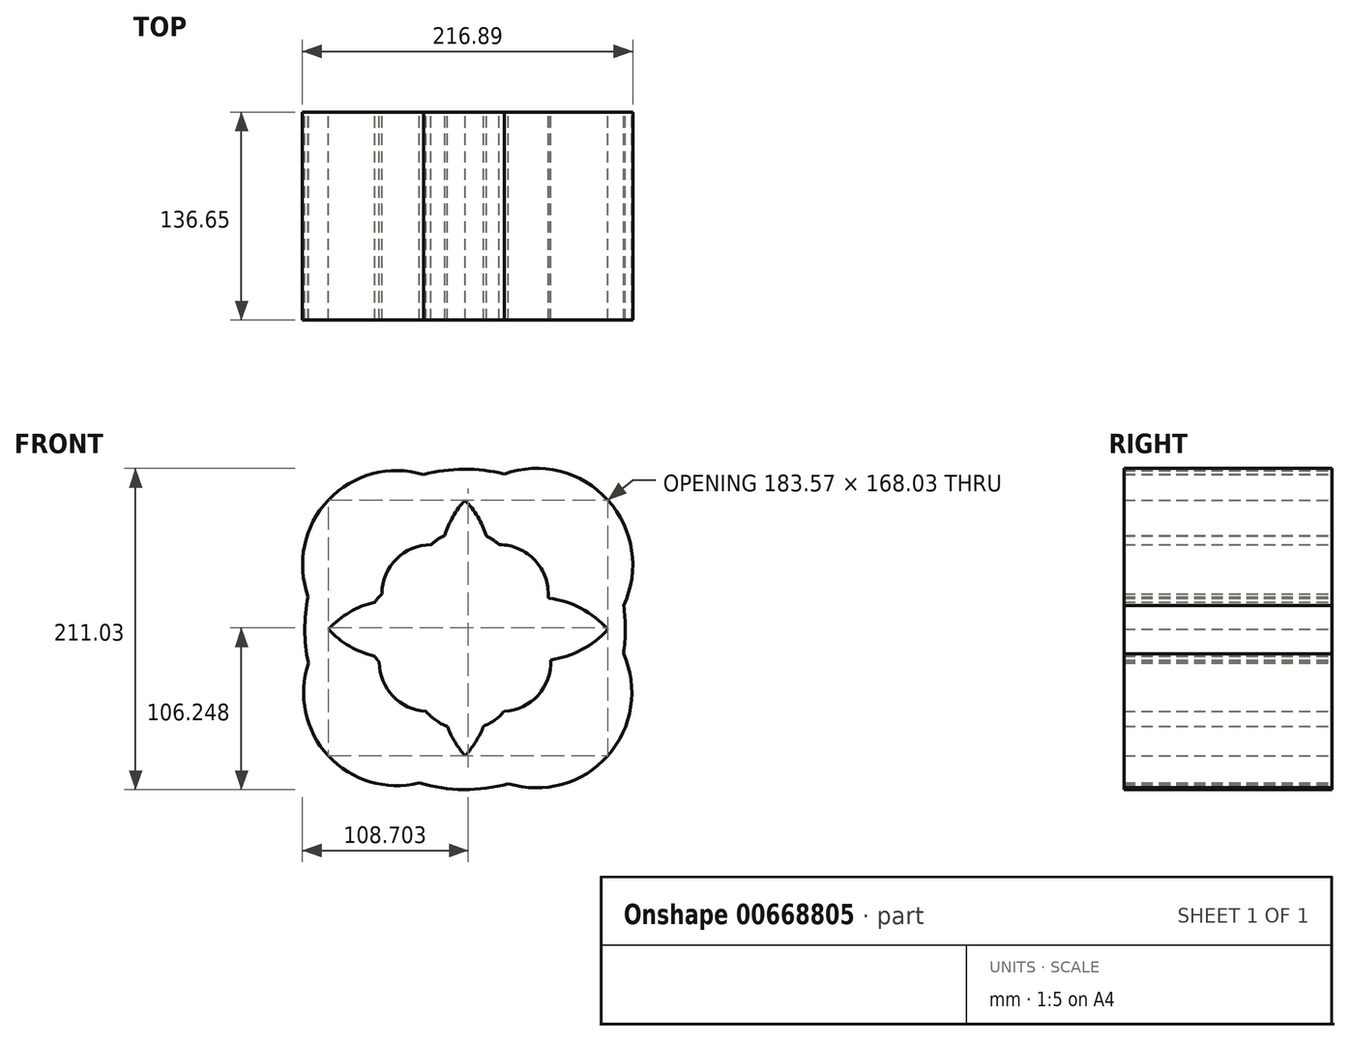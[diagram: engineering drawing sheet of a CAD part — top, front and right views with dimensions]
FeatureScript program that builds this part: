
annotation { "Feature Type Name" : "Feature", "Feature Type Description" : "" }
export const myFeature = defineFeature(function(context is Context, id is Id, definition is map)
    precondition{}
    {
        {
            var Q0;
            Q0=qCreatedBy(makeId("Front.planeOp"),FACE);
            var sketch = newSketch(context, id + "F0", { "sketchPlane" : qUnion([Q0])});
            skCircle(sketch, "E0", {"center": v(0, 0) * mm, "radius": 1.72 * mm});
            skCircle(sketch, "E1", {"center": v(0, 0) * mm, "radius": 1.24 * mm});
            skCircle(sketch, "E2", {"center": v(-44.92, 42.5) * mm, "radius": 61.84 * mm});
            skCircle(sketch, "E3", {"center": v(46.86, -41.52) * mm, "radius": 62.61 * mm});
            skCircle(sketch, "E4", {"center": v(46.86, 42.5) * mm, "radius": 63.26 * mm});
            skCircle(sketch, "E5", {"center": v(-44.92, -41.52) * mm, "radius": 61.17 * mm});
            skCircle(sketch, "E6", {"center": v(0, 0) * mm, "radius": 32.3 * mm});
            skCircle(sketch, "E7", {"center": v(-24.02, -21.6) * mm, "radius": 32.3 * mm});
            skCircle(sketch, "E8", {"center": v(-22.32, 23.35) * mm, "radius": 32.3 * mm});
            skCircle(sketch, "E9", {"center": v(22.32, 23.35) * mm, "radius": 32.3 * mm});
            skCircle(sketch, "E10", {"center": v(24.02, -21.6) * mm, "radius": 32.3 * mm});
            skCircle(sketch, "E11", {"center": v(0, 0) * mm, "radius": 105.28 * mm});
            skCircle(sketch, "E12", {"center": v(0, 32.3) * mm, "radius": 32.3 * mm});
            skCircle(sketch, "E13", {"center": v(-32.3, 0) * mm, "radius": 32.3 * mm});
            skCircle(sketch, "E14", {"center": v(0, -32.3) * mm, "radius": 33.53 * mm});
            skCircle(sketch, "E15", {"center": v(32.3, 0) * mm, "radius": 30.58 * mm});
            skSolve(sketch);
        }
        {
            var Q0;
            Q0 = qSketchRegion(id + "F0", true);
            extrude(context, id + "F1", {"entities" : qUnion([Q0]), "depth" : 136.65 * mm, "offsetDistance" : 25.4 * mm});
        }
    });
